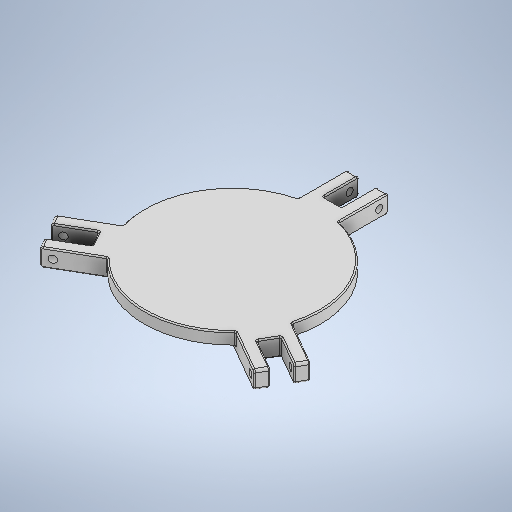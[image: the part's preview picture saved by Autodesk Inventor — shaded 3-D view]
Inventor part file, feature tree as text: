
AUTODESK INVENTOR PART (.ipt)
format: ipt  version: 2025.3 (Build 293356000, 356)  size: 502,784 bytes
history: native  units: in
note: dims shown in document units (in); Inventor stores cm internally (conversion verified against a paired STEP export)
features: sketch x6, fillet x4, hole x3, extrude x2
ambient origin geometry x8: Origin, YZ Plane, XZ Plane, XY Plane, X Axis, Y Axis, Z Axis, Center Point
bodies: Solid1 (feature_tree)
feature tree (15):
  extrude  "Extrusion1"  Depth=0.3937in TaperAngle=0.0deg
  extrude  "Extrusion2"  Depth=1.9685in
  hole  "Hole1"  [1 undecoded]
  hole  "Hole2"  [1 undecoded]
  hole  "Hole3"  [1 undecoded]
  fillet  "Fillet1"  Radius=0.315in
  fillet  "Fillet2"  Radius=0.8661in
  fillet  "Fillet3"  Radius=0.315in
  fillet  "Fillet4"  Radius=0.0787in
  sketch  "Sketch1"  dims[d0=5.9055in d1=0.3937in d2=0.0in]
  sketch  "Sketch2"  dims[d5=1.378in d6=1.1811in]
  sketch  "Sketch Circular Pattern1"  dims[d3=2.5591in d4=1.9685in]
  sketch  "Sketch3"  dims[d7=0.5906in d8=0.5906in d9=0.0in]
  sketch  "Sketch4"  dims[d10=1.1811in d12=360.0deg d14=0.315in]
  sketch  "Sketch5"  dims[d15=0.2362in d16=0.2362in d17=0.1575in d18=0.0787in d19=90.0deg d20=0.315in d21=0.8108in d22=0.315in d23=0.8661in d24=0.2362in d25=0.2362in d26=0.1575in d27=0.0787in d28=90.0deg d29=0.315in d30=0.8108in d31=0.315in d32=0.2362in d33=0.2362in d34=0.1575in d35=0.0787in d36=90.0deg d37=0.315in d38=0.8108in d39=0.0787in d40=0.0394in d41=0.0394in d42=0.0394in]
note: 3 required parameter values undecoded (feature->parameter linkage not recoverable at this tier; creation-order binding heuristic only, values carry confidence <= 0.55)
